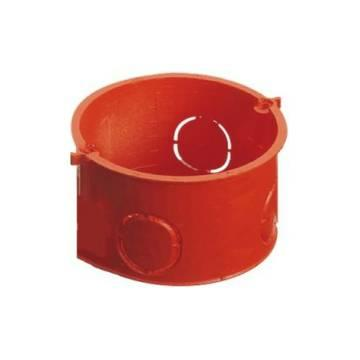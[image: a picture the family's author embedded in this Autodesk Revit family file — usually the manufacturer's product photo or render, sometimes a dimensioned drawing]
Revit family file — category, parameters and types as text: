
# Revit family: Building-FlushMountingEnclosures-GEWISS-24SC-BOXES_ROUND
name_source: partatom
category: Apparecchi elettrici
revit_build: Autodesk Revit 2016 (Build: 20161004_0715(x64)
units: mm (PartAtom-declared; Revit-internal decimal feet)

## family parameters
Condiviso = Sì
Host = Muro
Mantenere orientamento annotazione = Sì
Numero OmniClass = 23.80.30.14.24
Punto di calcolo locali = Sì
Quota connettore circolare = Usa diametro
Sempre verticale = Sì
Taglio con vuoti quando caricato = Sì
Tipo di parte = Normale
Titolo OmniClass = Junction Boxes

## types (2) — shared parameters
Catalogue = BUILDING
Catalogue Range = 24SC
Characteristics = Halogen free
Description: = Cylindrical
Diametro = 85 mm  [stored 0.278871 ft]
Diametro interno = 80 mm  [stored 0.262467 ft]
Electrocod = 0210
For walls = Masonry
Glow Wire Test = 650°C
IDF = 630946bf-62ab-4bbb-bc27-bc676e26c2fa
IDT = e9e05727-a289-4381-9e61-a78239658332
Immagine tipo = GW24210.jpg
Installation = Flush mounting enclosures
Operating temperature = -15 ÷ +60°C
Produttore = GEWISS S.p.A.
Profondità = 42 mm  [stored 0.137795 ft]
Profondità interna = 37 mm  [stored 0.121391 ft]
SEO = Box
Technical sheet = https://www.gewiss.com
Thermo-pressure with ball = 70
URL = https://www.gewiss.com
Version file RFA = 19.0

## per-type parameters (varying)
| type | Descrizione | Dimensions (mm) | EAN code | Modello |
| GW24209 - Round f.m.box D.65mm | ROUND F.M.BOX D.65X38 | Ã˜ 65x38 | 8011564016712 | GW24209 |
| GW24210 - Round f.m.box D.85mm | ROUND F.M.BOX D.85X42 | Ã˜ 85x42 | 8011564016736 | GW24210 |

note: source unit labels omitted for Thermo-pressure with ball — the stored unit's dimension contradicts the parameter name (converter mislabeling)

note: [stored X ft] marks values corroborated as IEEE doubles in the binary element streams (Revit-internal decimal feet)
